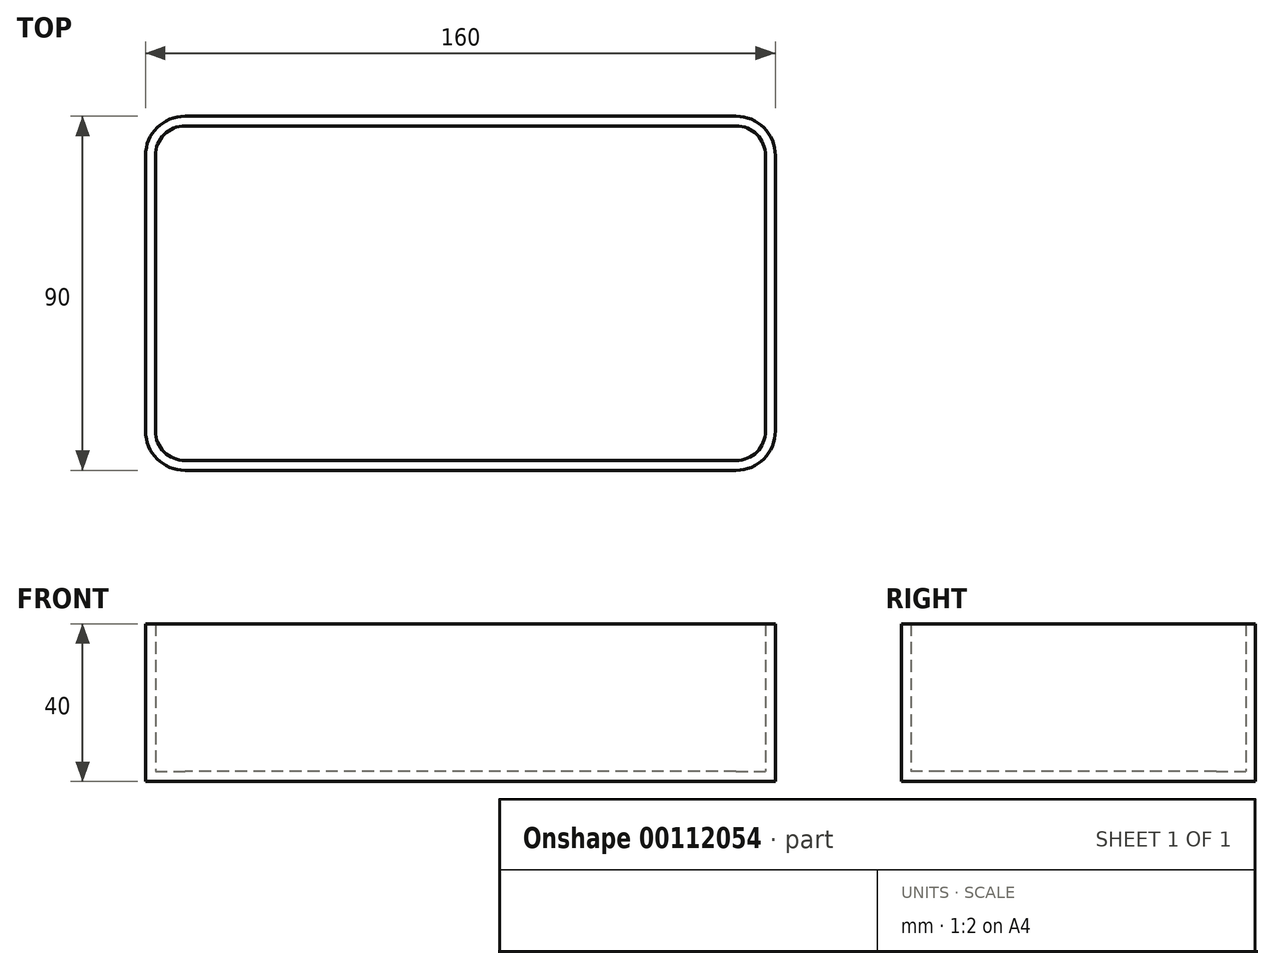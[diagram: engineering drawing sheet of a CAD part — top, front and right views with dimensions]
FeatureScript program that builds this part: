
annotation { "Feature Type Name" : "Feature", "Feature Type Description" : "" }
export const myFeature = defineFeature(function(context is Context, id is Id, definition is map)
    precondition{}
    {
        {
            var Q0;
            Q0=qCreatedBy(makeId("Top.planeOp"),FACE);
            var sketch = newSketch(context, id + "F0", { "sketchPlane" : qUnion([Q0])});
            skLineSegment(sketch, "E0.bottom", {"start": v(0, 0) * mm, "end": v(-160, 0) * mm});
            skLineSegment(sketch, "E0.top", {"start": v(0, -90) * mm, "end": v(-160, -90) * mm});
            skLineSegment(sketch, "E0.left", {"start": v(0, 0) * mm, "end": v(0, -90) * mm});
            skLineSegment(sketch, "E0.right", {"start": v(-160, 0) * mm, "end": v(-160, -90) * mm});
            skSolve(sketch);
        }
        {
            var Q0;
            Q0=makeQuery(id+"F0.imprint","IMPRINT",FACE,{"disambiguationData":[TD([[makeQuery(id+"F0.imprint","IMPRINT",EDGE,{"derivedFrom":sQuery(id+"F0.wireOp",EDGE,"E0.bottom")}),1.0]])]});
            extrude(context, id + "F1", {"entities" : qUnion([Q0]), "depth" : 40 * mm});
        }
        {
            var Q0;
            Q0=makeQuery(id+"F1.opExtrude","SWEPT_EDGE",EDGE,{"disambiguationData":[OSD([sQuery(id+"F0.wireOp",EDGE,"E0.top"),sQuery(id+"F0.wireOp",EDGE,"E0.right")])]});
            var Q1;
            Q1=makeQuery(id+"F1.opExtrude","SWEPT_EDGE",EDGE,{"disambiguationData":[OSD([sQuery(id+"F0.wireOp",EDGE,"E0.bottom"),sQuery(id+"F0.wireOp",EDGE,"E0.left")])]});
            var Q2;
            Q2=makeQuery(id+"F1.opExtrude","SWEPT_EDGE",EDGE,{"disambiguationData":[OSD([sQuery(id+"F0.wireOp",EDGE,"E0.top"),sQuery(id+"F0.wireOp",EDGE,"E0.left")])]});
            var Q3;
            Q3=makeQuery(id+"F1.opExtrude","SWEPT_EDGE",EDGE,{"disambiguationData":[OSD([sQuery(id+"F0.wireOp",EDGE,"E0.bottom"),sQuery(id+"F0.wireOp",EDGE,"E0.right")])]});
            fillet(context, id + "F2", {"entities" : qUnion([Q0, Q1, Q2, Q3]), "radius" : 10 * mm, "tangentPropagation" : true, "allowEdgeOverflow" : false});
        }
        {
            var Q0;
            Q0=makeQuery(id+"F1.opExtrude","CAP_FACE",FACE,{"disambiguationData":[OSD([sQuery(id+"F0.wireOp",EDGE,"E0.bottom"),sQuery(id+"F0.wireOp",EDGE,"E0.top"),sQuery(id+"F0.wireOp",EDGE,"E0.left"),sQuery(id+"F0.wireOp",EDGE,"E0.right")])],"isStart":false});
            shell(context, id + "F3", {"entities" : qUnion([Q0]), "thickness" : 2.5 * mm});
        }
    });
